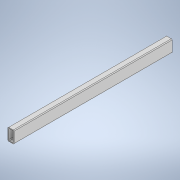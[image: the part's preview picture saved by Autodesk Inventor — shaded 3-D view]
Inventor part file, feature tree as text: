
AUTODESK INVENTOR PART (.ipt)
format: ipt  version: 2020 (Build 240168000, 168)  size: 125,440 bytes
history: native  units: in
note: dims shown in document units (in); Inventor stores cm internally (conversion verified against a paired STEP export)
features: extrude x1, sketch x1
ambient origin geometry x8: Origin, YZ Plane, XZ Plane, XY Plane, X Axis, Y Axis, Z Axis, Center Point
bodies: Solid1 (feature_tree)
feature tree (2):
  extrude  "Extrusion1"  Depth=1.0in
  sketch  "Sketch1"  dims[d0=2.0in d1=1.0in d2=0.125in d3=0.125in d4=0.125in d5=0.125in d6=0.125in d7=0.125in d8=0.125in d9=0.125in d10=0.125in d11=26.0in d12=0.0in]
